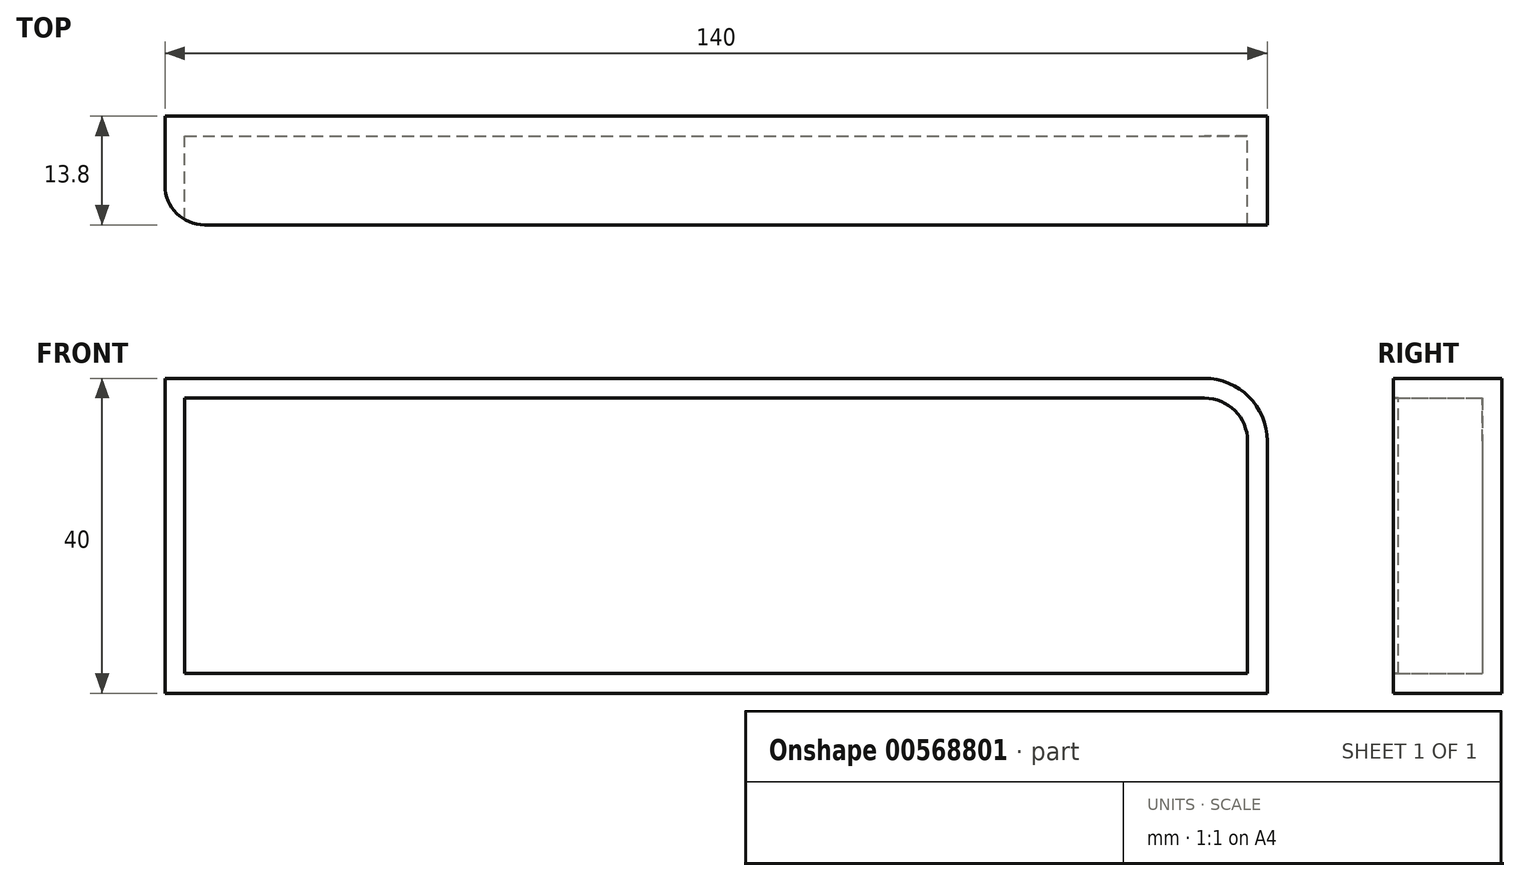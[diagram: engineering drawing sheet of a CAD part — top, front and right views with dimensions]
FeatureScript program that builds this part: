
annotation { "Feature Type Name" : "Feature", "Feature Type Description" : "" }
export const myFeature = defineFeature(function(context is Context, id is Id, definition is map)
    precondition{}
    {
        {
            var Q0;
            Q0=qCreatedBy(makeId("Front.planeOp"),FACE);
            var sketch = newSketch(context, id + "F0", { "sketchPlane" : qUnion([Q0])});
            skLineSegment(sketch, "E0.bottom", {"start": v(-70.08, 24.62) * mm, "end": v(69.92, 24.62) * mm});
            skLineSegment(sketch, "E0.top", {"start": v(-70.08, -15.38) * mm, "end": v(69.92, -15.38) * mm});
            skLineSegment(sketch, "E0.left", {"start": v(-70.08, 24.62) * mm, "end": v(-70.08, -15.38) * mm});
            skLineSegment(sketch, "E0.right", {"start": v(69.92, 24.62) * mm, "end": v(69.92, -15.38) * mm});
            skSolve(sketch);
        }
        {
            var Q0;
            Q0=makeQuery(id+"F0.imprint","IMPRINT",FACE,{"disambiguationData":[TD([[makeQuery(id+"F0.imprint","IMPRINT",EDGE,{"derivedFrom":sQuery(id+"F0.wireOp",EDGE,"E0.bottom")}),-1.0]])]});
            extrude(context, id + "F1", {"entities" : qUnion([Q0]), "depth" : 13.8 * mm, "offsetDistance" : 25 * mm});
        }
        {
            var Q0;
            Q0=makeQuery(id+"F1.opExtrude","SWEPT_EDGE",EDGE,{"disambiguationData":[OSD([sQuery(id+"F0.wireOp",EDGE,"E0.bottom"),sQuery(id+"F0.wireOp",EDGE,"E0.right")])]});
            fillet(context, id + "F2", {"entities" : qUnion([Q0]), "radius" : 7.97 * mm, "tangentPropagation" : true, "allowEdgeOverflow" : false});
        }
        {
            var Q0;
            Q0=makeQuery(id+"F1.opExtrude","CAP_FACE",FACE,{"disambiguationData":[OSD([sQuery(id+"F0.wireOp",EDGE,"E0.bottom"),sQuery(id+"F0.wireOp",EDGE,"E0.top"),sQuery(id+"F0.wireOp",EDGE,"E0.left"),sQuery(id+"F0.wireOp",EDGE,"E0.right")])],"isStart":false});
            shell(context, id + "F3", {"entities" : qUnion([Q0]), "thickness" : 2.5 * mm});
        }
        {
            var Q0;
            Q0=makeQuery(id+"F1.opExtrude","CAP_EDGE",EDGE,{"disambiguationData":[OSD([sQuery(id+"F0.wireOp",EDGE,"E0.left")])],"isStart":false});
            fillet(context, id + "F4", {"entities" : qUnion([Q0]), "radius" : 5 * mm, "tangentPropagation" : true, "allowEdgeOverflow" : false});
        }
    });
